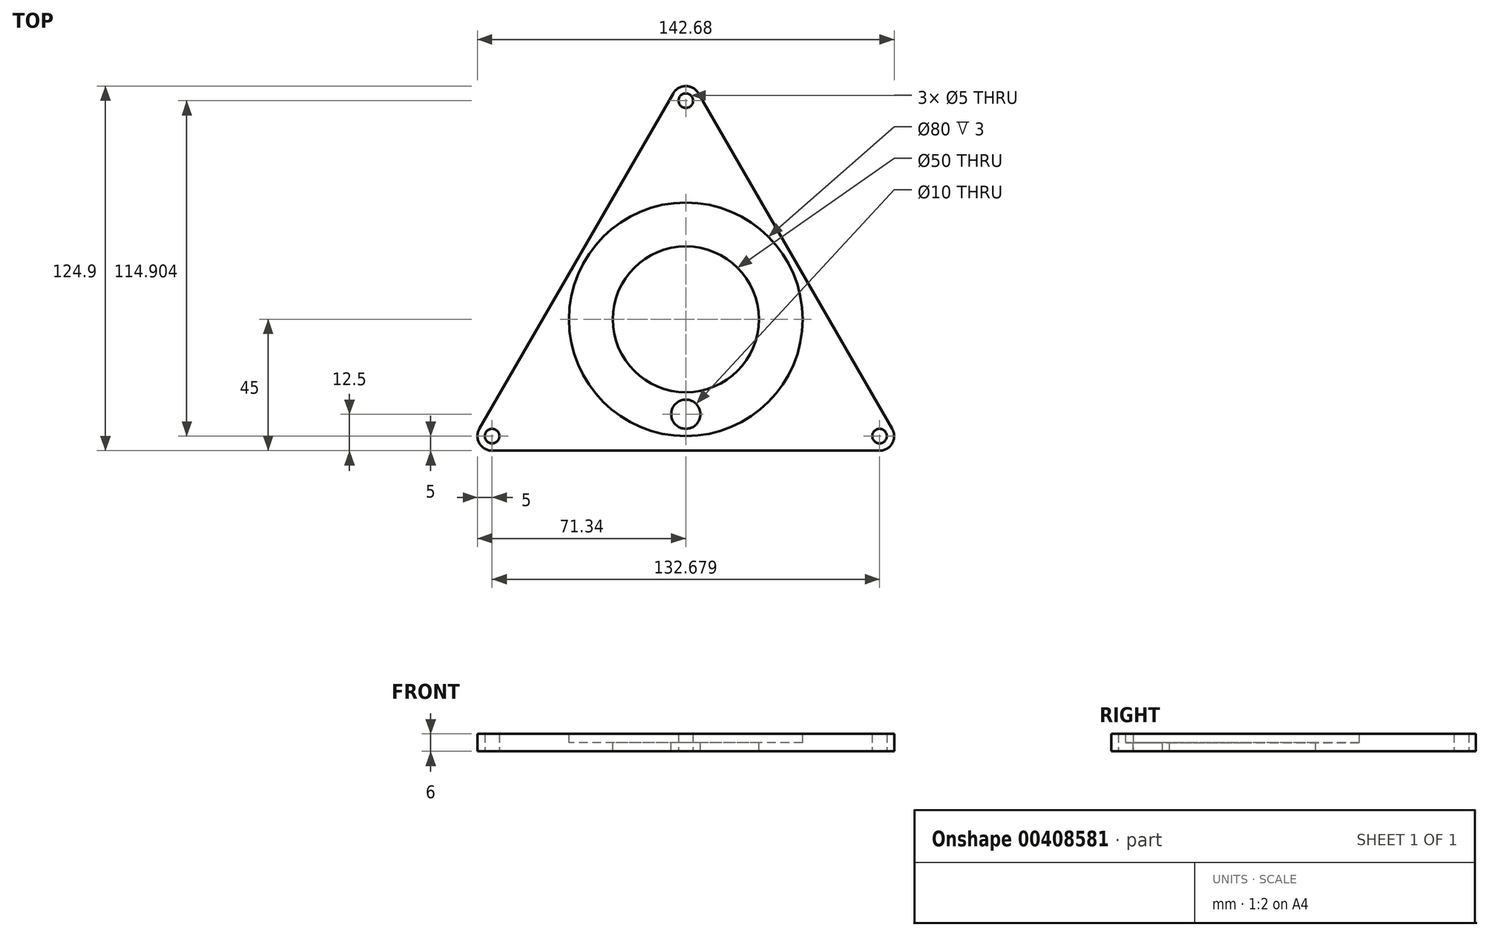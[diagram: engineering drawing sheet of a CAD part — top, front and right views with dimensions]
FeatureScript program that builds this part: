
annotation { "Feature Type Name" : "Feature", "Feature Type Description" : "" }
export const myFeature = defineFeature(function(context is Context, id is Id, definition is map)
    precondition{}
    {
        {
            var Q0;
            Q0=qCreatedBy(makeId("Top.planeOp"),FACE);
            var sketch = newSketch(context, id + "F0", { "sketchPlane" : qUnion([Q0])});
            skLineSegment(sketch, "E0", {"start": v(-4.33, 72.4) * mm, "end": v(-70.67, -42.5) * mm});
            skLineSegment(sketch, "E1", {"start": v(-66.34, -50) * mm, "end": v(66.34, -50) * mm});
            skLineSegment(sketch, "E2", {"start": v(70.67, -42.5) * mm, "end": v(4.33, 72.4) * mm});
            skPoint(sketch, "E3.visualSharp", {"position": v(0, 79.9) * mm});
            skArc(sketch, "E3.filletArc", {"start": v(4.33, 72.4) * mm, "mid": v(0, 74.9) * mm, "end": v(-4.33, 72.4) * mm});
            skPoint(sketch, "E4.visualSharp", {"position": v(-75, -50) * mm});
            skArc(sketch, "E4.filletArc", {"start": v(-70.67, -42.5) * mm, "mid": v(-70.67, -47.5) * mm, "end": v(-66.34, -50) * mm});
            skPoint(sketch, "E5.visualSharp", {"position": v(75, -50) * mm});
            skArc(sketch, "E5.filletArc", {"start": v(66.34, -50) * mm, "mid": v(70.67, -47.5) * mm, "end": v(70.67, -42.5) * mm});
            skCircle(sketch, "E6", {"center": v(0, 69.9) * mm, "radius": 2.5 * mm});
            skCircle(sketch, "E7", {"center": v(-66.34, -45) * mm, "radius": 2.5 * mm});
            skCircle(sketch, "E8", {"center": v(66.34, -45) * mm, "radius": 2.5 * mm});
            skSolve(sketch);
        }
        {
            var Q0;
            Q0=makeQuery(id+"F0.imprint","IMPRINT",FACE,{"disambiguationData":[TD([[makeQuery(id+"F0.imprint","IMPRINT",EDGE,{"derivedFrom":sQuery(id+"F0.wireOp",EDGE,"E0")}),1.0]])]});
            extrude(context, id + "F1", {"entities" : qUnion([Q0]), "depth" : 6 * mm, "offsetDistance" : 25 * mm});
        }
        {
            var Q0;
            Q0=makeQuery(id+"F1.opExtrude","CAP_FACE",FACE,{"disambiguationData":[OSD([sQuery(id+"F0.wireOp",EDGE,"E0"),sQuery(id+"F0.wireOp",EDGE,"E1"),sQuery(id+"F0.wireOp",EDGE,"E2"),sQuery(id+"F0.wireOp",EDGE,"E3.filletArc"),sQuery(id+"F0.wireOp",EDGE,"E4.filletArc"),sQuery(id+"F0.wireOp",EDGE,"E5.filletArc"),sQuery(id+"F0.wireOp",EDGE,"E6"),sQuery(id+"F0.wireOp",EDGE,"E7"),sQuery(id+"F0.wireOp",EDGE,"E8")])],"isStart":false});
            var sketch = newSketch(context, id + "F2", { "sketchPlane" : qUnion([Q0])});
            skCircle(sketch, "E9", {"center": v(0, -5) * mm, "radius": 40 * mm});
            skSolve(sketch);
        }
        {
            var Q0;
            Q0=makeQuery(id+"F2.imprint","IMPRINT",FACE,{"disambiguationData":[TD([[makeQuery(id+"F2.imprint","IMPRINT",EDGE,{"derivedFrom":sQuery(id+"F2.wireOp",EDGE,"E9")}),1.0]])]});
            extrude(context, id + "F3", {"entities" : qUnion([Q0]), "operationType" : NewBodyOperationType.REMOVE, "oppositeDirection" : true, "depth" : 3 * mm, "offsetDistance" : 25 * mm});
        }
        {
            var Q0;
            Q0=makeQuery(id+"F3.boolean.opBoolean","COPY",FACE,{"derivedFrom":makeQuery(id+"F3.opExtrude","CAP_FACE",FACE,{"disambiguationData":[OSD([sQuery(id+"F2.wireOp",EDGE,"E9")])],"isStart":false})});
            var sketch = newSketch(context, id + "F4", { "sketchPlane" : qUnion([Q0])});
            skCircle(sketch, "E10", {"center": v(0, -5) * mm, "radius": 25 * mm});
            skSolve(sketch);
        }
        {
            var Q0;
            Q0 = qSketchRegion(id + "F4", true);
            extrude(context, id + "F5", {"entities" : qUnion([Q0]), "operationType" : NewBodyOperationType.REMOVE, "oppositeDirection" : true, "depth" : 25 * mm, "offsetDistance" : 25 * mm});
        }
        {
            var Q0;
            Q0=makeQuery(id+"F3.boolean.opBoolean","COPY",FACE,{"derivedFrom":makeQuery(id+"F3.opExtrude","CAP_FACE",FACE,{"disambiguationData":[OSD([sQuery(id+"F2.wireOp",EDGE,"E9")])],"isStart":false})});
            var sketch = newSketch(context, id + "F6", { "sketchPlane" : qUnion([Q0])});
            skCircle(sketch, "E11", {"center": v(0, -37.5) * mm, "radius": 5 * mm});
            skSolve(sketch);
        }
        {
            var Q0;
            Q0=makeQuery(id+"F6.imprint","IMPRINT",FACE,{"disambiguationData":[TD([[makeQuery(id+"F6.imprint","IMPRINT",EDGE,{"derivedFrom":sQuery(id+"F6.wireOp",EDGE,"E11")}),1.0]])]});
            extrude(context, id + "F7", {"entities" : qUnion([Q0]), "operationType" : NewBodyOperationType.REMOVE, "oppositeDirection" : true, "depth" : 25 * mm, "offsetDistance" : 25 * mm});
        }
    });
